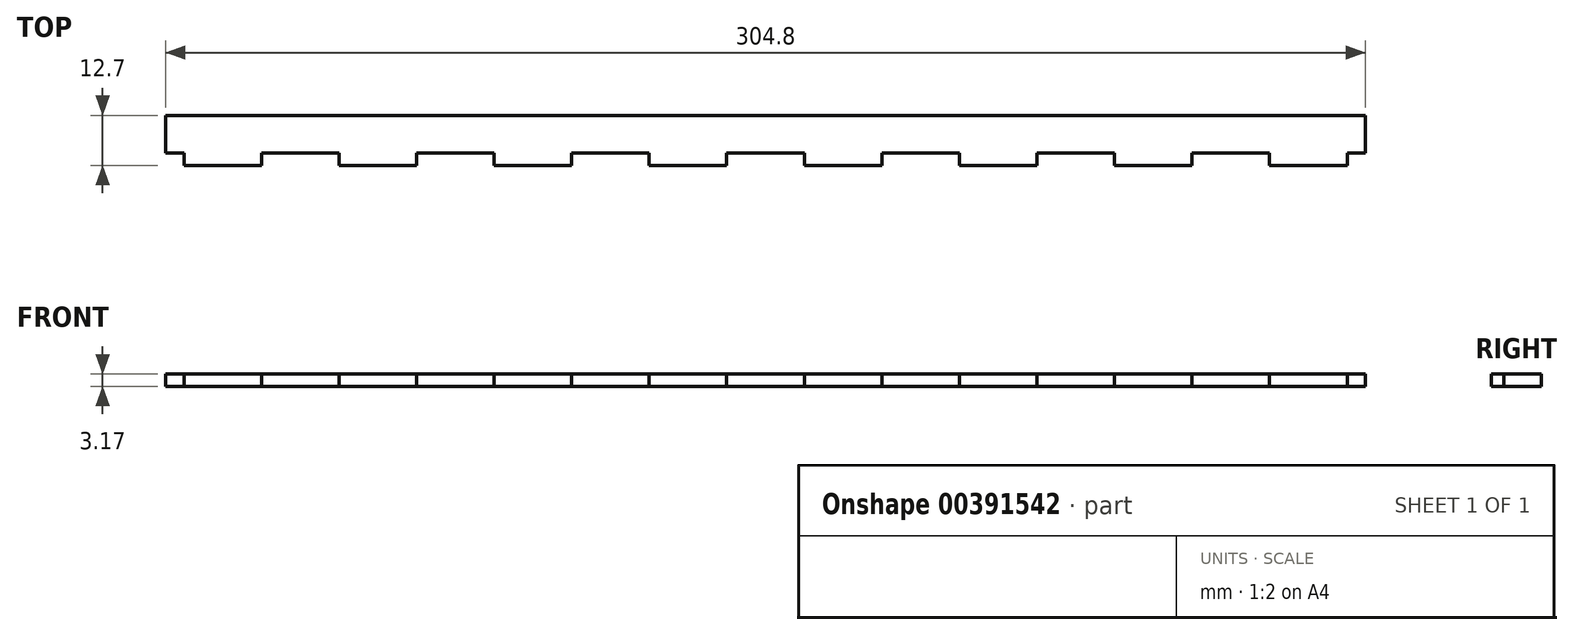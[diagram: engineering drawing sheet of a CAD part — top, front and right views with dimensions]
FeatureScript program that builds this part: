
annotation { "Feature Type Name" : "Feature", "Feature Type Description" : "" }
export const myFeature = defineFeature(function(context is Context, id is Id, definition is map)
    precondition{}
    {
        {
            var Q0;
            Q0=qCreatedBy(makeId("Top.planeOp"),FACE);
            var sketch = newSketch(context, id + "F0", { "sketchPlane" : qUnion([Q0])});
            skLineSegment(sketch, "E0.right", {"start": v(-384.18, -158.75) * mm, "end": v(-384.18, 158.75) * mm, "construction": true});
            skPoint(sketch, "E0.middle", {"position": v(0, 0) * mm});
            skLineSegment(sketch, "E1.bottom", {"start": v(-384.18, 158.75) * mm, "end": v(-364.47, 158.75) * mm});
            skLineSegment(sketch, "E1.left", {"start": v(-384.18, 158.75) * mm, "end": v(-384.18, 142.04) * mm});
            skLineSegment(sketch, "E2.right", {"start": v(-381, 142.04) * mm, "end": v(-381, 125.33) * mm});
            skLineSegment(sketch, "E3", {"start": v(-384.18, 142.04) * mm, "end": v(-381, 142.04) * mm});
            skLineSegment(sketch, "E4", {"start": v(-364.47, 158.75) * mm, "end": v(-364.47, 155.57) * mm});
            skLineSegment(sketch, "E5", {"start": v(-364.47, 155.57) * mm, "end": v(-344.77, 155.57) * mm});
            skLineSegment(sketch, "E6", {"start": v(384.18, 158.75) * mm, "end": v(-384.18, 158.75) * mm, "construction": true});
            skLineSegment(sketch, "E7", {"start": v(-381, 125.33) * mm, "end": v(-384.18, 125.33) * mm});
            skLineSegment(sketch, "E8.1.0.1", {"start": v(-384.18, 108.62) * mm, "end": v(-381, 108.62) * mm});
            skLineSegment(sketch, "E8.1.0.3", {"start": v(-384.17, 125.33) * mm, "end": v(-384.18, 108.62) * mm});
            skLineSegment(sketch, "E8.4.0.0", {"start": v(-381, -8.36) * mm, "end": v(-384.17, -8.36) * mm});
            skLineSegment(sketch, "E8.4.0.1", {"start": v(-384.17, 8.36) * mm, "end": v(-381, 8.36) * mm});
            skLineSegment(sketch, "E8.4.0.2", {"start": v(-381, 8.36) * mm, "end": v(-381, -8.36) * mm});
            skLineSegment(sketch, "E8.7.0.0", {"start": v(-381, -108.62) * mm, "end": v(-384.17, -108.62) * mm});
            skLineSegment(sketch, "E8.8.0.0", {"start": v(-381, -142.04) * mm, "end": v(-384.17, -142.04) * mm});
            skLineSegment(sketch, "E8.8.0.1", {"start": v(-384.17, -125.33) * mm, "end": v(-381, -125.33) * mm});
            skLineSegment(sketch, "E8.8.0.2", {"start": v(-381, -125.33) * mm, "end": v(-381, -142.04) * mm});
            skLineSegment(sketch, "E8.8.0.3", {"start": v(-384.17, -108.62) * mm, "end": v(-384.17, -125.33) * mm});
            skLineSegment(sketch, "E8.9.0.1", {"start": v(-384.17, -158.75) * mm, "end": v(-381, -158.75) * mm});
            skLineSegment(sketch, "E8.9.0.3", {"start": v(-384.17, -142.04) * mm, "end": v(-384.17, -158.75) * mm});
            skLineSegment(sketch, "E8.direction1", {"start": v(-384.18, 125.33) * mm, "end": v(-384.18, 91.9) * mm, "construction": true});
            skLineSegment(sketch, "E9", {"start": v(-344.77, 155.57) * mm, "end": v(-344.77, 158.75) * mm});
            skLineSegment(sketch, "E10.1.0.0", {"start": v(-325.07, 158.75) * mm, "end": v(-325.07, 155.58) * mm});
            skLineSegment(sketch, "E10.1.0.1", {"start": v(-325.07, 155.58) * mm, "end": v(-305.37, 155.58) * mm});
            skLineSegment(sketch, "E10.1.0.2", {"start": v(-305.37, 155.58) * mm, "end": v(-305.37, 158.75) * mm});
            skLineSegment(sketch, "E10.1.0.3", {"start": v(-344.77, 158.75) * mm, "end": v(-325.07, 158.75) * mm});
            skLineSegment(sketch, "E10.2.0.0", {"start": v(-285.67, 158.75) * mm, "end": v(-285.67, 155.58) * mm});
            skLineSegment(sketch, "E10.2.0.1", {"start": v(-285.67, 155.58) * mm, "end": v(-265.97, 155.58) * mm});
            skLineSegment(sketch, "E10.2.0.2", {"start": v(-265.97, 155.58) * mm, "end": v(-265.97, 158.75) * mm});
            skLineSegment(sketch, "E10.2.0.3", {"start": v(-305.37, 158.75) * mm, "end": v(-285.67, 158.75) * mm});
            skLineSegment(sketch, "E10.3.0.0", {"start": v(-246.27, 158.75) * mm, "end": v(-246.27, 155.58) * mm});
            skLineSegment(sketch, "E10.3.0.1", {"start": v(-246.27, 155.58) * mm, "end": v(-226.56, 155.58) * mm});
            skLineSegment(sketch, "E10.3.0.2", {"start": v(-226.56, 155.58) * mm, "end": v(-226.56, 158.75) * mm});
            skLineSegment(sketch, "E10.3.0.3", {"start": v(-265.97, 158.75) * mm, "end": v(-246.27, 158.75) * mm});
            skLineSegment(sketch, "E10.4.0.0", {"start": v(-206.86, 158.75) * mm, "end": v(-206.86, 155.58) * mm});
            skLineSegment(sketch, "E10.4.0.1", {"start": v(-206.86, 155.58) * mm, "end": v(-187.16, 155.58) * mm});
            skLineSegment(sketch, "E10.4.0.2", {"start": v(-187.16, 155.58) * mm, "end": v(-187.16, 158.75) * mm});
            skLineSegment(sketch, "E10.4.0.3", {"start": v(-226.56, 158.75) * mm, "end": v(-206.86, 158.75) * mm});
            skLineSegment(sketch, "E10.5.0.0", {"start": v(-167.46, 158.75) * mm, "end": v(-167.46, 155.58) * mm});
            skLineSegment(sketch, "E10.5.0.1", {"start": v(-167.46, 155.58) * mm, "end": v(-147.76, 155.58) * mm});
            skLineSegment(sketch, "E10.5.0.2", {"start": v(-147.76, 155.58) * mm, "end": v(-147.76, 158.75) * mm});
            skLineSegment(sketch, "E10.5.0.3", {"start": v(-187.16, 158.75) * mm, "end": v(-167.46, 158.75) * mm});
            skLineSegment(sketch, "E10.6.0.0", {"start": v(-128.06, 158.75) * mm, "end": v(-128.06, 155.58) * mm});
            skLineSegment(sketch, "E10.6.0.1", {"start": v(-128.06, 155.58) * mm, "end": v(-108.36, 155.58) * mm});
            skLineSegment(sketch, "E10.6.0.2", {"start": v(-108.36, 155.58) * mm, "end": v(-108.36, 158.75) * mm});
            skLineSegment(sketch, "E10.6.0.3", {"start": v(-147.76, 158.75) * mm, "end": v(-128.06, 158.75) * mm});
            skLineSegment(sketch, "E10.7.0.0", {"start": v(-88.66, 158.75) * mm, "end": v(-88.66, 155.58) * mm});
            skLineSegment(sketch, "E10.7.0.1", {"start": v(-88.66, 155.58) * mm, "end": v(-68.95, 155.58) * mm});
            skLineSegment(sketch, "E10.7.0.2", {"start": v(-68.95, 155.58) * mm, "end": v(-68.95, 158.75) * mm});
            skLineSegment(sketch, "E10.7.0.3", {"start": v(-108.36, 158.75) * mm, "end": v(-88.66, 158.75) * mm});
            skLineSegment(sketch, "E10.8.0.0", {"start": v(-49.25, 158.75) * mm, "end": v(-49.25, 155.58) * mm});
            skLineSegment(sketch, "E10.8.0.1", {"start": v(-49.25, 155.58) * mm, "end": v(-29.55, 155.58) * mm});
            skLineSegment(sketch, "E10.8.0.2", {"start": v(-29.55, 155.58) * mm, "end": v(-29.55, 158.75) * mm});
            skLineSegment(sketch, "E10.8.0.3", {"start": v(-68.95, 158.75) * mm, "end": v(-49.25, 158.75) * mm});
            skLineSegment(sketch, "E10.9.0.0", {"start": v(-9.85, 158.75) * mm, "end": v(-9.85, 155.58) * mm});
            skLineSegment(sketch, "E10.9.0.1", {"start": v(-9.85, 155.58) * mm, "end": v(9.85, 155.58) * mm});
            skLineSegment(sketch, "E10.9.0.2", {"start": v(9.85, 155.58) * mm, "end": v(9.85, 158.75) * mm});
            skLineSegment(sketch, "E10.9.0.3", {"start": v(-29.55, 158.75) * mm, "end": v(-9.85, 158.75) * mm});
            skLineSegment(sketch, "E10.10.0.0", {"start": v(29.55, 158.75) * mm, "end": v(29.55, 155.58) * mm});
            skLineSegment(sketch, "E10.10.0.1", {"start": v(29.55, 155.58) * mm, "end": v(49.25, 155.58) * mm});
            skLineSegment(sketch, "E10.10.0.2", {"start": v(49.25, 155.58) * mm, "end": v(49.25, 158.75) * mm});
            skLineSegment(sketch, "E10.10.0.3", {"start": v(9.85, 158.75) * mm, "end": v(29.55, 158.75) * mm});
            skLineSegment(sketch, "E10.11.0.0", {"start": v(68.95, 158.75) * mm, "end": v(68.95, 155.58) * mm});
            skLineSegment(sketch, "E10.11.0.1", {"start": v(68.95, 155.58) * mm, "end": v(88.66, 155.58) * mm});
            skLineSegment(sketch, "E10.11.0.2", {"start": v(88.66, 155.58) * mm, "end": v(88.66, 158.75) * mm});
            skLineSegment(sketch, "E10.11.0.3", {"start": v(49.25, 158.75) * mm, "end": v(68.95, 158.75) * mm});
            skLineSegment(sketch, "E10.12.0.0", {"start": v(108.36, 158.75) * mm, "end": v(108.36, 155.58) * mm});
            skLineSegment(sketch, "E10.12.0.3", {"start": v(88.66, 158.75) * mm, "end": v(108.36, 158.75) * mm});
            skLineSegment(sketch, "E10.16.0.2", {"start": v(285.67, 155.58) * mm, "end": v(285.67, 158.75) * mm});
            skLineSegment(sketch, "E10.17.0.0", {"start": v(305.37, 158.75) * mm, "end": v(305.37, 155.58) * mm});
            skLineSegment(sketch, "E10.17.0.1", {"start": v(305.37, 155.58) * mm, "end": v(325.07, 155.58) * mm});
            skLineSegment(sketch, "E10.17.0.2", {"start": v(325.07, 155.58) * mm, "end": v(325.07, 158.75) * mm});
            skLineSegment(sketch, "E10.17.0.3", {"start": v(285.67, 158.75) * mm, "end": v(305.37, 158.75) * mm});
            skLineSegment(sketch, "E10.18.0.0", {"start": v(344.77, 158.75) * mm, "end": v(344.77, 155.58) * mm});
            skLineSegment(sketch, "E10.18.0.1", {"start": v(344.77, 155.58) * mm, "end": v(364.47, 155.58) * mm});
            skLineSegment(sketch, "E10.18.0.2", {"start": v(364.47, 155.58) * mm, "end": v(364.47, 158.75) * mm});
            skLineSegment(sketch, "E10.18.0.3", {"start": v(325.07, 158.75) * mm, "end": v(344.77, 158.75) * mm});
            skLineSegment(sketch, "E10.19.0.0", {"start": v(384.18, 158.75) * mm, "end": v(384.18, 155.58) * mm});
            skLineSegment(sketch, "E10.19.0.3", {"start": v(364.47, 158.75) * mm, "end": v(384.18, 158.75) * mm});
            skLineSegment(sketch, "E10.direction1", {"start": v(-384.18, 158.75) * mm, "end": v(-344.77, 158.75) * mm, "construction": true});
            skLineSegment(sketch, "E11.MirrorCS", {"start": v(384.18, -158.75) * mm, "end": v(384.18, -155.58) * mm});
            skLineSegment(sketch, "E12.MirrorCS", {"start": v(-344.77, -155.57) * mm, "end": v(-344.77, -158.75) * mm});
            skLineSegment(sketch, "E13.MirrorCS", {"start": v(108.36, -158.75) * mm, "end": v(108.36, -155.58) * mm});
            skLineSegment(sketch, "E14.MirrorCS", {"start": v(285.67, -155.58) * mm, "end": v(285.67, -158.75) * mm});
            skLineSegment(sketch, "E15.MirrorCS", {"start": v(-285.67, -158.75) * mm, "end": v(-285.67, -155.58) * mm});
            skLineSegment(sketch, "E16.MirrorCS", {"start": v(49.25, -155.58) * mm, "end": v(49.25, -158.75) * mm});
            skLineSegment(sketch, "E17.MirrorCS", {"start": v(-108.36, -155.58) * mm, "end": v(-108.36, -158.75) * mm});
            skLineSegment(sketch, "E18.MirrorCS", {"start": v(-265.97, -155.58) * mm, "end": v(-265.97, -158.75) * mm});
            skLineSegment(sketch, "E19.MirrorCS", {"start": v(-29.55, -155.58) * mm, "end": v(-29.55, -158.75) * mm});
            skLineSegment(sketch, "E20.MirrorCS", {"start": v(364.47, -155.58) * mm, "end": v(364.47, -158.75) * mm});
            skLineSegment(sketch, "E21.MirrorCS", {"start": v(-206.86, -158.75) * mm, "end": v(-206.86, -155.58) * mm});
            skLineSegment(sketch, "E22.MirrorCS", {"start": v(-147.76, -155.58) * mm, "end": v(-147.76, -158.75) * mm});
            skLineSegment(sketch, "E23.MirrorCS", {"start": v(-305.37, -155.58) * mm, "end": v(-305.37, -158.75) * mm});
            skLineSegment(sketch, "E24.MirrorCS", {"start": v(206.86, -155.58) * mm, "end": v(206.86, -158.75) * mm});
            skLineSegment(sketch, "E25.MirrorCS", {"start": v(344.77, -158.75) * mm, "end": v(344.77, -155.58) * mm});
            skLineSegment(sketch, "E26.MirrorCS", {"start": v(128.06, -155.58) * mm, "end": v(128.06, -158.75) * mm});
            skLineSegment(sketch, "E27.MirrorCS", {"start": v(9.85, -155.58) * mm, "end": v(9.85, -158.75) * mm});
            skLineSegment(sketch, "E28.MirrorCS", {"start": v(-364.47, -158.75) * mm, "end": v(-364.47, -155.57) * mm});
            skLineSegment(sketch, "E29.MirrorCS", {"start": v(325.07, -155.58) * mm, "end": v(325.07, -158.75) * mm});
            skLineSegment(sketch, "E30.MirrorCS", {"start": v(167.46, -155.58) * mm, "end": v(167.46, -158.75) * mm});
            skLineSegment(sketch, "E31.MirrorCS", {"start": v(147.76, -158.75) * mm, "end": v(147.76, -155.58) * mm});
            skLineSegment(sketch, "E32.MirrorCS", {"start": v(305.37, -158.75) * mm, "end": v(305.37, -155.58) * mm});
            skLineSegment(sketch, "E33.MirrorCS", {"start": v(-88.66, -158.75) * mm, "end": v(-88.66, -155.58) * mm});
            skLineSegment(sketch, "E34.MirrorCS", {"start": v(29.55, -158.75) * mm, "end": v(29.55, -155.58) * mm});
            skLineSegment(sketch, "E35.MirrorCS", {"start": v(-128.06, -158.75) * mm, "end": v(-128.06, -155.58) * mm});
            skLineSegment(sketch, "E36.MirrorCS", {"start": v(-226.56, -155.58) * mm, "end": v(-226.56, -158.75) * mm});
            skLineSegment(sketch, "E37.MirrorCS", {"start": v(88.66, -155.58) * mm, "end": v(88.66, -158.75) * mm});
            skLineSegment(sketch, "E38.MirrorCS", {"start": v(246.27, -155.58) * mm, "end": v(246.27, -158.75) * mm});
            skLineSegment(sketch, "E39.MirrorCS", {"start": v(-68.95, -155.58) * mm, "end": v(-68.95, -158.75) * mm});
            skLineSegment(sketch, "E40.MirrorCS", {"start": v(265.97, -158.75) * mm, "end": v(265.97, -155.58) * mm});
            skLineSegment(sketch, "E41.MirrorCS", {"start": v(-325.07, -158.75) * mm, "end": v(-325.07, -155.58) * mm});
            skLineSegment(sketch, "E42.MirrorCS", {"start": v(187.16, -158.75) * mm, "end": v(187.16, -155.58) * mm});
            skLineSegment(sketch, "E43.MirrorCS", {"start": v(-187.16, -155.58) * mm, "end": v(-187.16, -158.75) * mm});
            skLineSegment(sketch, "E44.MirrorCS", {"start": v(-167.46, -158.75) * mm, "end": v(-167.46, -155.58) * mm});
            skLineSegment(sketch, "E45.MirrorCS", {"start": v(-9.85, -158.75) * mm, "end": v(-9.85, -155.58) * mm});
            skLineSegment(sketch, "E46.MirrorCS", {"start": v(-246.27, -158.75) * mm, "end": v(-246.27, -155.58) * mm});
            skLineSegment(sketch, "E47.MirrorCS", {"start": v(226.56, -158.75) * mm, "end": v(226.56, -155.58) * mm});
            skLineSegment(sketch, "E48.MirrorCS", {"start": v(68.95, -158.75) * mm, "end": v(68.95, -155.58) * mm});
            skLineSegment(sketch, "E49.MirrorCS", {"start": v(-49.25, -158.75) * mm, "end": v(-49.25, -155.58) * mm});
            skLineSegment(sketch, "E50.MirrorCS", {"start": v(-68.95, -158.75) * mm, "end": v(-49.25, -158.75) * mm});
            skLineSegment(sketch, "E51.MirrorCS", {"start": v(-226.56, -158.75) * mm, "end": v(-206.86, -158.75) * mm});
            skLineSegment(sketch, "E52.MirrorCS", {"start": v(246.27, -158.75) * mm, "end": v(265.97, -158.75) * mm});
            skLineSegment(sketch, "E53.MirrorCS", {"start": v(206.86, -158.75) * mm, "end": v(226.56, -158.75) * mm});
            skLineSegment(sketch, "E54.MirrorCS", {"start": v(49.25, -158.75) * mm, "end": v(68.95, -158.75) * mm});
            skLineSegment(sketch, "E55.MirrorCS", {"start": v(-265.97, -158.75) * mm, "end": v(-246.27, -158.75) * mm});
            skLineSegment(sketch, "E56.MirrorCS", {"start": v(-108.36, -158.75) * mm, "end": v(-88.66, -158.75) * mm});
            skLineSegment(sketch, "E57.MirrorCS", {"start": v(88.66, -158.75) * mm, "end": v(108.36, -158.75) * mm});
            skLineSegment(sketch, "E58.MirrorCS", {"start": v(-344.77, -158.75) * mm, "end": v(-325.07, -158.75) * mm});
            skLineSegment(sketch, "E59.MirrorCS", {"start": v(285.67, -158.75) * mm, "end": v(305.37, -158.75) * mm});
            skLineSegment(sketch, "E60.MirrorCS", {"start": v(128.06, -158.75) * mm, "end": v(147.76, -158.75) * mm});
            skLineSegment(sketch, "E61.MirrorCS", {"start": v(-384.18, -158.75) * mm, "end": v(-364.47, -158.75) * mm});
            skLineSegment(sketch, "E62.MirrorCS", {"start": v(167.46, -158.75) * mm, "end": v(187.16, -158.75) * mm});
            skLineSegment(sketch, "E63.MirrorCS", {"start": v(325.07, -158.75) * mm, "end": v(344.77, -158.75) * mm});
            skLineSegment(sketch, "E64.MirrorCS", {"start": v(364.47, -158.75) * mm, "end": v(384.18, -158.75) * mm});
            skLineSegment(sketch, "E65.MirrorCS", {"start": v(-29.55, -158.75) * mm, "end": v(-9.85, -158.75) * mm});
            skLineSegment(sketch, "E66.MirrorCS", {"start": v(-187.16, -158.75) * mm, "end": v(-167.46, -158.75) * mm});
            skLineSegment(sketch, "E67.MirrorCS", {"start": v(-305.37, -158.75) * mm, "end": v(-285.67, -158.75) * mm});
            skLineSegment(sketch, "E68.MirrorCS", {"start": v(-147.76, -158.75) * mm, "end": v(-128.06, -158.75) * mm});
            skLineSegment(sketch, "E69.MirrorCS", {"start": v(9.85, -158.75) * mm, "end": v(29.55, -158.75) * mm});
            skLineSegment(sketch, "E70.MirrorCS", {"start": v(29.55, -155.58) * mm, "end": v(49.25, -155.58) * mm});
            skLineSegment(sketch, "E71.MirrorCS", {"start": v(226.56, -155.58) * mm, "end": v(246.27, -155.58) * mm});
            skLineSegment(sketch, "E72.MirrorCS", {"start": v(-88.66, -155.58) * mm, "end": v(-68.95, -155.58) * mm});
            skLineSegment(sketch, "E73.MirrorCS", {"start": v(-49.25, -155.58) * mm, "end": v(-29.55, -155.58) * mm});
            skLineSegment(sketch, "E74.MirrorCS", {"start": v(-206.86, -155.58) * mm, "end": v(-187.16, -155.58) * mm});
            skLineSegment(sketch, "E75.MirrorCS", {"start": v(-364.47, -155.57) * mm, "end": v(-344.77, -155.57) * mm});
            skLineSegment(sketch, "E76.MirrorCS", {"start": v(384.18, -158.75) * mm, "end": v(-384.18, -158.75) * mm, "construction": true});
            skLineSegment(sketch, "E77.MirrorCS", {"start": v(-128.06, -155.58) * mm, "end": v(-108.36, -155.58) * mm});
            skLineSegment(sketch, "E78.MirrorCS", {"start": v(-285.67, -155.58) * mm, "end": v(-265.97, -155.58) * mm});
            skLineSegment(sketch, "E79.MirrorCS", {"start": v(344.77, -155.58) * mm, "end": v(364.47, -155.58) * mm});
            skLineSegment(sketch, "E80.MirrorCS", {"start": v(-9.85, -155.58) * mm, "end": v(9.85, -155.58) * mm});
            skLineSegment(sketch, "E81.MirrorCS", {"start": v(-167.46, -155.58) * mm, "end": v(-147.76, -155.58) * mm});
            skLineSegment(sketch, "E82.MirrorCS", {"start": v(-325.07, -155.58) * mm, "end": v(-305.37, -155.58) * mm});
            skLineSegment(sketch, "E83.MirrorCS", {"start": v(305.37, -155.58) * mm, "end": v(325.07, -155.58) * mm});
            skLineSegment(sketch, "E84.MirrorCS", {"start": v(147.76, -155.58) * mm, "end": v(167.46, -155.58) * mm});
            skLineSegment(sketch, "E85.MirrorCS", {"start": v(265.97, -155.58) * mm, "end": v(285.67, -155.58) * mm});
            skLineSegment(sketch, "E86.MirrorCS", {"start": v(-246.27, -155.58) * mm, "end": v(-226.56, -155.58) * mm});
            skLineSegment(sketch, "E87.MirrorCS", {"start": v(68.95, -155.58) * mm, "end": v(88.66, -155.58) * mm});
            skLineSegment(sketch, "E88.MirrorCS", {"start": v(187.16, -155.58) * mm, "end": v(206.86, -155.58) * mm});
            skLineSegment(sketch, "E89.MirrorCS", {"start": v(-384.18, -158.75) * mm, "end": v(-344.77, -158.75) * mm, "construction": true});
            skLineSegment(sketch, "E90.MirrorCS", {"start": v(108.36, -155.58) * mm, "end": v(128.06, -155.58) * mm});
            skLineSegment(sketch, "E91.MirrorCS", {"start": v(384.17, -158.75) * mm, "end": v(381, -158.75) * mm});
            skLineSegment(sketch, "E92.MirrorCS", {"start": v(384.18, 108.62) * mm, "end": v(381, 108.62) * mm});
            skLineSegment(sketch, "E93.MirrorCS", {"start": v(381, 125.33) * mm, "end": v(384.18, 125.33) * mm});
            skLineSegment(sketch, "E94.MirrorCS", {"start": v(381, -108.62) * mm, "end": v(384.17, -108.62) * mm});
            skLineSegment(sketch, "E95.MirrorCS", {"start": v(384.18, 142.04) * mm, "end": v(381, 142.04) * mm});
            skLineSegment(sketch, "E96.MirrorCS", {"start": v(381, -142.04) * mm, "end": v(384.17, -142.04) * mm});
            skLineSegment(sketch, "E97.MirrorCS", {"start": v(384.17, 8.36) * mm, "end": v(381, 8.36) * mm});
            skLineSegment(sketch, "E98.MirrorCS", {"start": v(384.17, -125.33) * mm, "end": v(381, -125.33) * mm});
            skLineSegment(sketch, "E99.MirrorCS", {"start": v(384.17, 125.33) * mm, "end": v(384.18, 108.62) * mm});
            skLineSegment(sketch, "E100.MirrorCS", {"start": v(381, -8.36) * mm, "end": v(384.17, -8.36) * mm});
            skLineSegment(sketch, "E101.MirrorCS", {"start": v(384.17, -142.04) * mm, "end": v(384.17, -158.75) * mm});
            skLineSegment(sketch, "E102.MirrorCS", {"start": v(384.18, 158.75) * mm, "end": v(384.18, 142.04) * mm});
            skLineSegment(sketch, "E103.MirrorCS", {"start": v(384.17, -108.62) * mm, "end": v(384.17, -125.33) * mm});
            skLineSegment(sketch, "E104.MirrorCS", {"start": v(381, 142.04) * mm, "end": v(381, 125.33) * mm});
            skLineSegment(sketch, "E105.MirrorCS", {"start": v(381, 8.36) * mm, "end": v(381, -8.36) * mm});
            skLineSegment(sketch, "E106.MirrorCS", {"start": v(384.18, -158.75) * mm, "end": v(384.18, 158.75) * mm, "construction": true});
            skLineSegment(sketch, "E107.MirrorCS", {"start": v(381, -125.33) * mm, "end": v(381, -142.04) * mm});
            skLineSegment(sketch, "E108.bottom", {"start": v(371.48, -146.05) * mm, "end": v(-371.48, -146.05) * mm});
            skLineSegment(sketch, "E108.top", {"start": v(371.48, 146.05) * mm, "end": v(-371.48, 146.05) * mm});
            skLineSegment(sketch, "E108.left", {"start": v(371.48, -146.05) * mm, "end": v(371.48, 146.05) * mm});
            skLineSegment(sketch, "E108.right", {"start": v(-371.48, -146.05) * mm, "end": v(-371.48, 146.05) * mm});
            skLineSegment(sketch, "E109", {"start": v(353.63, -95.25) * mm, "end": v(314.49, -95.25) * mm, "construction": true});
            skLineSegment(sketch, "E110", {"start": v(314.51, -19.05) * mm, "end": v(356.15, -19.05) * mm, "construction": true});
            skLineSegment(sketch, "E111", {"start": v(317.24, 19.05) * mm, "end": v(357.03, 19.05) * mm, "construction": true});
            skLineSegment(sketch, "E112", {"start": v(317.78, 95.25) * mm, "end": v(359.55, 95.25) * mm, "construction": true});
            skLineSegment(sketch, "E113", {"start": v(381, -108.62) * mm, "end": v(381, -95.25) * mm});
            skLineSegment(sketch, "E114", {"start": v(384.18, -8.36) * mm, "end": v(384.18, -19.05) * mm});
            skLineSegment(sketch, "E115", {"start": v(381, -95.25) * mm, "end": v(371.48, -95.25) * mm});
            skLineSegment(sketch, "E116", {"start": v(384.18, -19.05) * mm, "end": v(371.48, -19.05) * mm});
            skLineSegment(sketch, "E117", {"start": v(384.17, 8.36) * mm, "end": v(384.18, 19.05) * mm});
            skLineSegment(sketch, "E118", {"start": v(381, 108.62) * mm, "end": v(381, 95.25) * mm});
            skLineSegment(sketch, "E119", {"start": v(384.18, 19.05) * mm, "end": v(371.48, 19.05) * mm});
            skLineSegment(sketch, "E120", {"start": v(381, 95.25) * mm, "end": v(371.48, 95.25) * mm});
            skLineSegment(sketch, "E121.MirrorCS", {"start": v(-314.51, -19.05) * mm, "end": v(-356.15, -19.05) * mm, "construction": true});
            skLineSegment(sketch, "E122.MirrorCS", {"start": v(-317.78, 95.25) * mm, "end": v(-359.55, 95.25) * mm, "construction": true});
            skLineSegment(sketch, "E123.MirrorCS", {"start": v(-353.63, -95.25) * mm, "end": v(-314.49, -95.25) * mm, "construction": true});
            skLineSegment(sketch, "E124.MirrorCS", {"start": v(-317.24, 19.05) * mm, "end": v(-357.03, 19.05) * mm, "construction": true});
            skLineSegment(sketch, "E125", {"start": v(-381, -108.62) * mm, "end": v(-381, -95.25) * mm});
            skLineSegment(sketch, "E126", {"start": v(-381, -95.25) * mm, "end": v(-371.48, -95.25) * mm});
            skLineSegment(sketch, "E127", {"start": v(-381, 108.62) * mm, "end": v(-381, 95.25) * mm});
            skLineSegment(sketch, "E128", {"start": v(-381, 95.25) * mm, "end": v(-371.48, 95.25) * mm});
            skLineSegment(sketch, "E129", {"start": v(-384.18, -8.36) * mm, "end": v(-384.18, -19.05) * mm});
            skLineSegment(sketch, "E130", {"start": v(-384.18, -19.05) * mm, "end": v(-371.48, -19.05) * mm});
            skLineSegment(sketch, "E131", {"start": v(104.78, 110.81) * mm, "end": v(104.78, 136.48) * mm, "construction": true});
            skLineSegment(sketch, "E132", {"start": v(168.28, 138.21) * mm, "end": v(168.28, 115.73) * mm, "construction": true});
            skLineSegment(sketch, "E133", {"start": v(108.36, 155.58) * mm, "end": v(111.13, 155.58) * mm});
            skLineSegment(sketch, "E134", {"start": v(285.67, 155.58) * mm, "end": v(268.6, 155.58) * mm});
            skLineSegment(sketch, "E135", {"start": v(-384.18, 19.05) * mm, "end": v(-384.17, 8.36) * mm});
            skLineSegment(sketch, "E136", {"start": v(-384.18, 19.05) * mm, "end": v(-371.48, 19.05) * mm});
            skLineSegment(sketch, "E137.MirrorCS", {"start": v(167.46, 155.58) * mm, "end": v(167.46, 158.75) * mm});
            skLineSegment(sketch, "E138.MirrorCS", {"start": v(147.76, 158.75) * mm, "end": v(147.76, 155.58) * mm});
            skLineSegment(sketch, "E139.MirrorCS", {"start": v(128.06, 155.58) * mm, "end": v(128.06, 158.75) * mm});
            skLineSegment(sketch, "E140.MirrorCS", {"start": v(265.97, 158.75) * mm, "end": v(265.97, 155.58) * mm});
            skLineSegment(sketch, "E141.MirrorCS", {"start": v(246.27, 155.58) * mm, "end": v(246.27, 158.75) * mm});
            skLineSegment(sketch, "E142.MirrorCS", {"start": v(226.56, 158.75) * mm, "end": v(226.56, 155.58) * mm});
            skLineSegment(sketch, "E143.MirrorCS", {"start": v(187.16, 158.75) * mm, "end": v(187.16, 155.58) * mm});
            skLineSegment(sketch, "E144.MirrorCS", {"start": v(206.86, 155.58) * mm, "end": v(206.86, 158.75) * mm});
            skLineSegment(sketch, "E145.MirrorCS", {"start": v(265.97, 155.58) * mm, "end": v(285.67, 155.58) * mm});
            skLineSegment(sketch, "E146.MirrorCS", {"start": v(206.86, 158.75) * mm, "end": v(226.56, 158.75) * mm});
            skLineSegment(sketch, "E147.MirrorCS", {"start": v(147.76, 155.58) * mm, "end": v(167.46, 155.58) * mm});
            skLineSegment(sketch, "E148.MirrorCS", {"start": v(246.27, 158.75) * mm, "end": v(265.97, 158.75) * mm});
            skLineSegment(sketch, "E149.MirrorCS", {"start": v(167.46, 158.75) * mm, "end": v(187.16, 158.75) * mm});
            skLineSegment(sketch, "E150.MirrorCS", {"start": v(128.06, 158.75) * mm, "end": v(147.76, 158.75) * mm});
            skLineSegment(sketch, "E151.MirrorCS", {"start": v(108.36, 155.58) * mm, "end": v(128.06, 155.58) * mm});
            skLineSegment(sketch, "E152.MirrorCS", {"start": v(187.16, 155.58) * mm, "end": v(206.86, 155.58) * mm});
            skLineSegment(sketch, "E153.MirrorCS", {"start": v(226.56, 155.58) * mm, "end": v(246.27, 155.58) * mm});
            skLineSegment(sketch, "E154", {"start": v(168.28, 138.21) * mm, "end": v(168.28, 188.5) * mm, "construction": true});
            skLineSegment(sketch, "E155.bottom", {"start": v(104.78, 110.81) * mm, "end": v(168.28, 110.81) * mm});
            skLineSegment(sketch, "E155.top", {"start": v(104.78, 188.5) * mm, "end": v(168.28, 188.5) * mm});
            skLineSegment(sketch, "E155.left", {"start": v(104.78, 110.81) * mm, "end": v(104.77, 188.5) * mm});
            skLineSegment(sketch, "E155.right", {"start": v(168.28, 110.81) * mm, "end": v(168.28, 188.5) * mm});
            skLineSegment(sketch, "E156", {"start": v(-436.86, 146.05) * mm, "end": v(-309.02, 146.05) * mm, "construction": true});
            skLineSegment(sketch, "E157.bottom", {"start": v(-436.86, 146.05) * mm, "end": v(-317.78, 146.05) * mm});
            skLineSegment(sketch, "E157.top", {"start": v(-436.86, 95.25) * mm, "end": v(-317.78, 95.25) * mm});
            skLineSegment(sketch, "E157.left", {"start": v(-436.86, 146.05) * mm, "end": v(-436.86, 95.25) * mm});
            skLineSegment(sketch, "E157.right", {"start": v(-317.78, 146.05) * mm, "end": v(-317.78, 95.25) * mm});
            skLineSegment(sketch, "E158", {"start": v(-152.4, -11.84) * mm, "end": v(-152.4, -292.06) * mm, "construction": true});
            skLineSegment(sketch, "E159", {"start": v(152.4, -4.45) * mm, "end": v(152.4, -285.28) * mm, "construction": true});
            skLineSegment(sketch, "E160", {"start": v(-152.4, -146.05) * mm, "end": v(-152.4, -155.58) * mm});
            skLineSegment(sketch, "E161", {"start": v(152.4, -146.05) * mm, "end": v(152.4, -155.58) * mm});
            skSolve(sketch);
        }
        {
            var Q0;
            Q0=makeQuery(id+"F0.imprint","IMPRINT",FACE,{"disambiguationData":[TD([[makeQuery(id+"F0.imprint","IMPRINT",EDGE,{"derivedFrom":sQuery(id+"F0.wireOp",EDGE,"E13.MirrorCS")}),1.0]])]});
            extrude(context, id + "F1", {"entities" : qUnion([Q0]), "depth" : 3.17 * mm});
        }
    });
